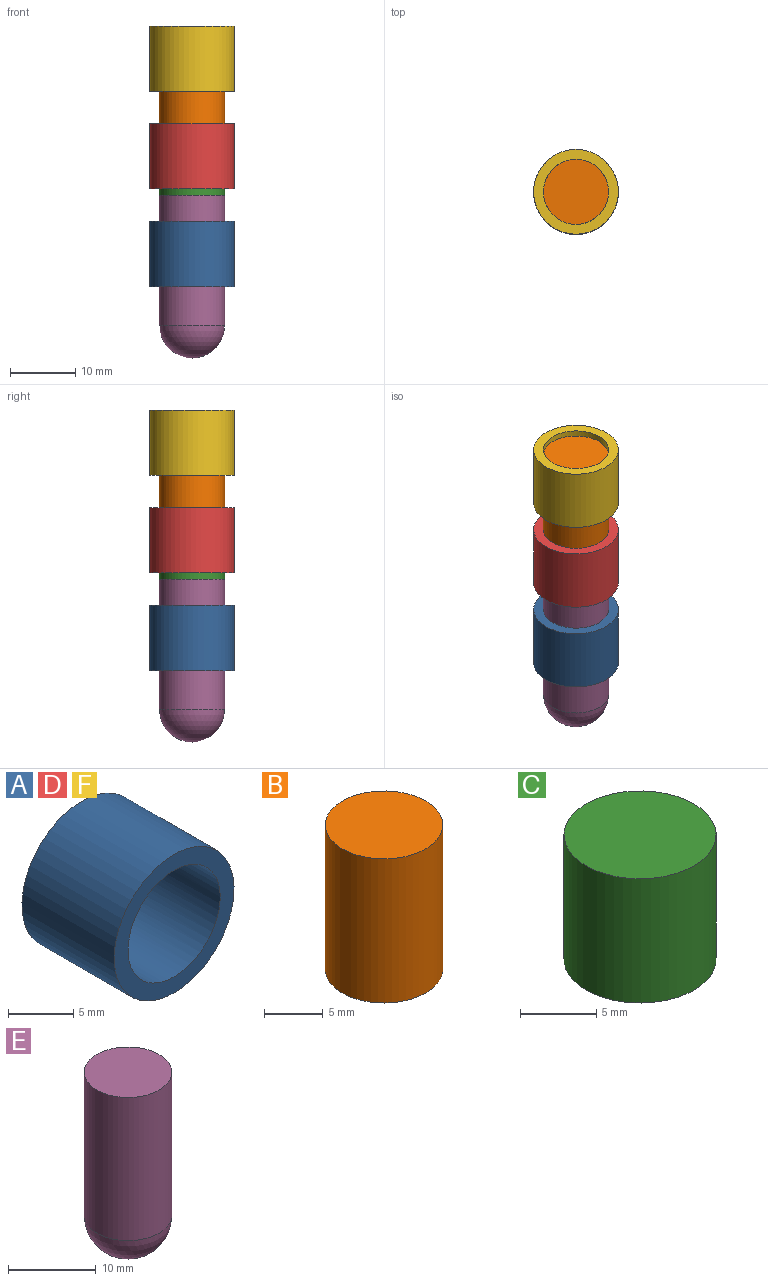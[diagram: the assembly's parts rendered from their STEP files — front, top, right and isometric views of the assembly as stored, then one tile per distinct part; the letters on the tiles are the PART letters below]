
ASSEMBLY  parts=6 mates=5
PART A: 4 faces, bbox 13x10x13 mm
  f0: cylinder r=6.5mm len=13mm, axis (0,1,0), area 408.4mm2, adj f1,f2
  f1: plane 13x13mm, normal (0,-1,0), area 54.2mm2, adj f0,f3
  f2: plane 13x13mm, normal (0,1,0), area 54.2mm2, adj f0,f3
  f3: cylinder r=5mm len=10mm, axis (0,1,0), area 314.2mm2, adj f1,f2
PART B: 3 faces, bbox 10x10x15 mm
  f0: cylinder r=5mm len=15mm, axis (0,0,-1), area 471.2mm2, adj f1,f2
  f1: plane 10x10mm, normal (0,0,1), area 78.5mm2, adj f0
  f2: plane 10x10mm, normal (0,0,-1), area 78.5mm2, adj f0
PART C: 3 faces, bbox 10x10x10 mm
  f0: cylinder r=5mm len=10mm, axis (0,0,-1), area 314.2mm2, adj f1,f2
  f1: plane 10x10mm, normal (0,0,1), area 78.5mm2, adj f0
  f2: plane 10x10mm, normal (0,0,-1), area 78.5mm2, adj f0
PART D: same geometry as A
PART E: 3 faces, bbox 10x10x25 mm
  f0: cylinder r=5mm len=20mm, axis (0,0,1), area 628.3mm2, adj f1,f2
  f1: plane 10x10mm, normal (0,0,1), area 78.5mm2, adj f0
  f2: sphere r=5mm, area 157.1mm2, adj f0
PART F: same geometry as A
PLACE A rot(axis=(1,0,0),90deg) t=(-23.27,-6.31,1.71)mm
PLACE B t=(-23.27,-6.31,5.76)mm
PLACE C t=(-23.27,-6.31,5.76)mm
PLACE D rot(axis=(-1,0,0),90deg) t=(-23.27,-6.31,6.71)mm
PLACE E t=(-23.27,-6.31,5.76)mm
PLACE F rot(axis=(1,0,0),90deg) t=(-23.27,-6.31,31.71)mm
MATE planar F.f0 <-> D.f0  axis (0,0,-1) through (-23.27,-6.31,21.71)mm
MATE slider A.f0 <-> E.f0  axis (0,0,1) through (-23.27,-6.31,-8.29)mm
MATE slider F.f0 <-> B.f0  axis (0,0,-1) through (-23.27,-6.31,21.71)mm
MATE slider D.f0 <-> C.f0  axis (0,0,-1) through (-23.27,-6.31,6.71)mm
MATE planar A.f0 <-> D.f0  axis (0,0,1) through (-23.27,-6.31,1.71)mm
